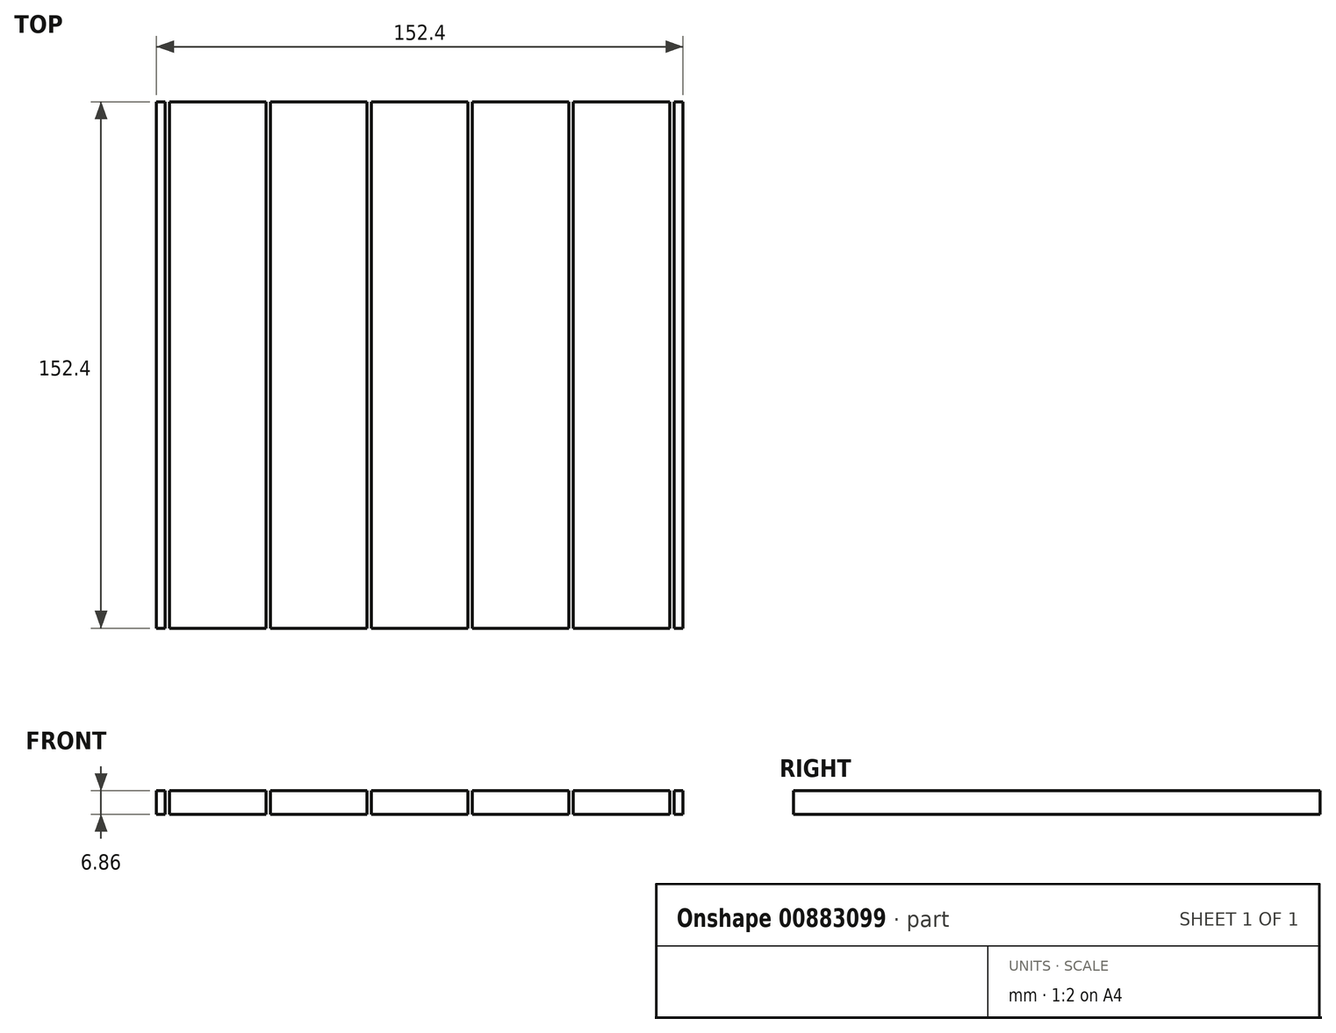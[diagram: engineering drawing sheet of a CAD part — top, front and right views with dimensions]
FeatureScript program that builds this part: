
annotation { "Feature Type Name" : "Feature", "Feature Type Description" : "" }
export const myFeature = defineFeature(function(context is Context, id is Id, definition is map)
    precondition{}
    {
        {
            var Q0;
            Q0=qCreatedBy(makeId("Top.planeOp"),FACE);
            var sketch = newSketch(context, id + "F0", { "sketchPlane" : qUnion([Q0])});
            skPoint(sketch, "E0.middle", {"position": v(0, 0) * mm});
            skLineSegment(sketch, "E1.bottom", {"start": v(76.2, 76.2) * mm, "end": v(73.66, 76.2) * mm});
            skLineSegment(sketch, "E1.top", {"start": v(76.2, -76.2) * mm, "end": v(73.66, -76.2) * mm});
            skLineSegment(sketch, "E1.left", {"start": v(76.2, 76.2) * mm, "end": v(76.2, -76.2) * mm});
            skLineSegment(sketch, "E1.right", {"start": v(-76.2, 76.2) * mm, "end": v(-76.2, -76.2) * mm});
            skLineSegment(sketch, "E2.bottom", {"start": v(13.97, 76.2) * mm, "end": v(-13.97, 76.2) * mm});
            skLineSegment(sketch, "E2.top", {"start": v(13.97, -76.2) * mm, "end": v(-13.97, -76.2) * mm});
            skLineSegment(sketch, "E2.left", {"start": v(13.97, 76.2) * mm, "end": v(13.97, -76.2) * mm});
            skLineSegment(sketch, "E2.right", {"start": v(-13.97, 76.2) * mm, "end": v(-13.97, -76.2) * mm});
            skLineSegment(sketch, "E3", {"start": v(-15.24, -76.2) * mm, "end": v(-15.24, 76.2) * mm});
            skLineSegment(sketch, "E4", {"start": v(15.24, -76.2) * mm, "end": v(15.24, 76.2) * mm});
            skLineSegment(sketch, "E5", {"start": v(-43.18, -76.2) * mm, "end": v(-43.18, 76.2) * mm});
            skLineSegment(sketch, "E6", {"start": v(-44.45, -76.2) * mm, "end": v(-44.45, 76.2) * mm});
            skLineSegment(sketch, "E7", {"start": v(43.18, -76.2) * mm, "end": v(43.18, 76.2) * mm});
            skLineSegment(sketch, "E8", {"start": v(44.45, -76.2) * mm, "end": v(44.45, 76.2) * mm});
            skLineSegment(sketch, "E9", {"start": v(72.39, -76.2) * mm, "end": v(72.39, 76.2) * mm});
            skLineSegment(sketch, "E10", {"start": v(-72.4, -76.2) * mm, "end": v(-72.4, 76.2) * mm});
            skLineSegment(sketch, "E11", {"start": v(-73.66, -76.2) * mm, "end": v(-73.66, 76.2) * mm});
            skLineSegment(sketch, "E12", {"start": v(73.66, -76.2) * mm, "end": v(73.66, 76.2) * mm});
            skLineSegment(sketch, "E13.trimOffspring", {"start": v(-73.66, 76.2) * mm, "end": v(-76.2, 76.2) * mm});
            skLineSegment(sketch, "E14.trimOffspring", {"start": v(-44.45, 76.2) * mm, "end": v(-72.4, 76.2) * mm});
            skLineSegment(sketch, "E15.trimOffspring", {"start": v(-15.24, 76.2) * mm, "end": v(-43.18, 76.2) * mm});
            skLineSegment(sketch, "E16.trimOffspring", {"start": v(43.18, 76.2) * mm, "end": v(15.24, 76.2) * mm});
            skLineSegment(sketch, "E17.trimOffspring", {"start": v(72.39, 76.2) * mm, "end": v(44.45, 76.2) * mm});
            skLineSegment(sketch, "E18.trimOffspring", {"start": v(72.39, -76.2) * mm, "end": v(44.45, -76.2) * mm});
            skLineSegment(sketch, "E19.trimOffspring", {"start": v(43.18, -76.2) * mm, "end": v(15.24, -76.2) * mm});
            skLineSegment(sketch, "E20.trimOffspring", {"start": v(-15.24, -76.2) * mm, "end": v(-43.18, -76.2) * mm});
            skLineSegment(sketch, "E21.trimOffspring", {"start": v(-44.45, -76.2) * mm, "end": v(-72.4, -76.2) * mm});
            skLineSegment(sketch, "E22.trimOffspring", {"start": v(-73.66, -76.2) * mm, "end": v(-76.2, -76.2) * mm});
            skLineSegment(sketch, "E23", {"start": v(71.12, 76.2) * mm, "end": v(71.12, -76.2) * mm, "construction": true});
            skLineSegment(sketch, "E24", {"start": v(45.72, 76.2) * mm, "end": v(45.72, -76.2) * mm, "construction": true});
            skLineSegment(sketch, "E25", {"start": v(41.9, 76.2) * mm, "end": v(41.9, -76.2) * mm, "construction": true});
            skSolve(sketch);
        }
        {
            var Q0;
            Q0 = qSketchRegion(id + "F0", true);
            extrude(context, id + "F1", {"entities" : qUnion([Q0]), "endBound" : BoundingType.SYMMETRIC, "depth" : 6.86 * mm, "offsetDistance" : 25.4 * mm});
        }
    });
